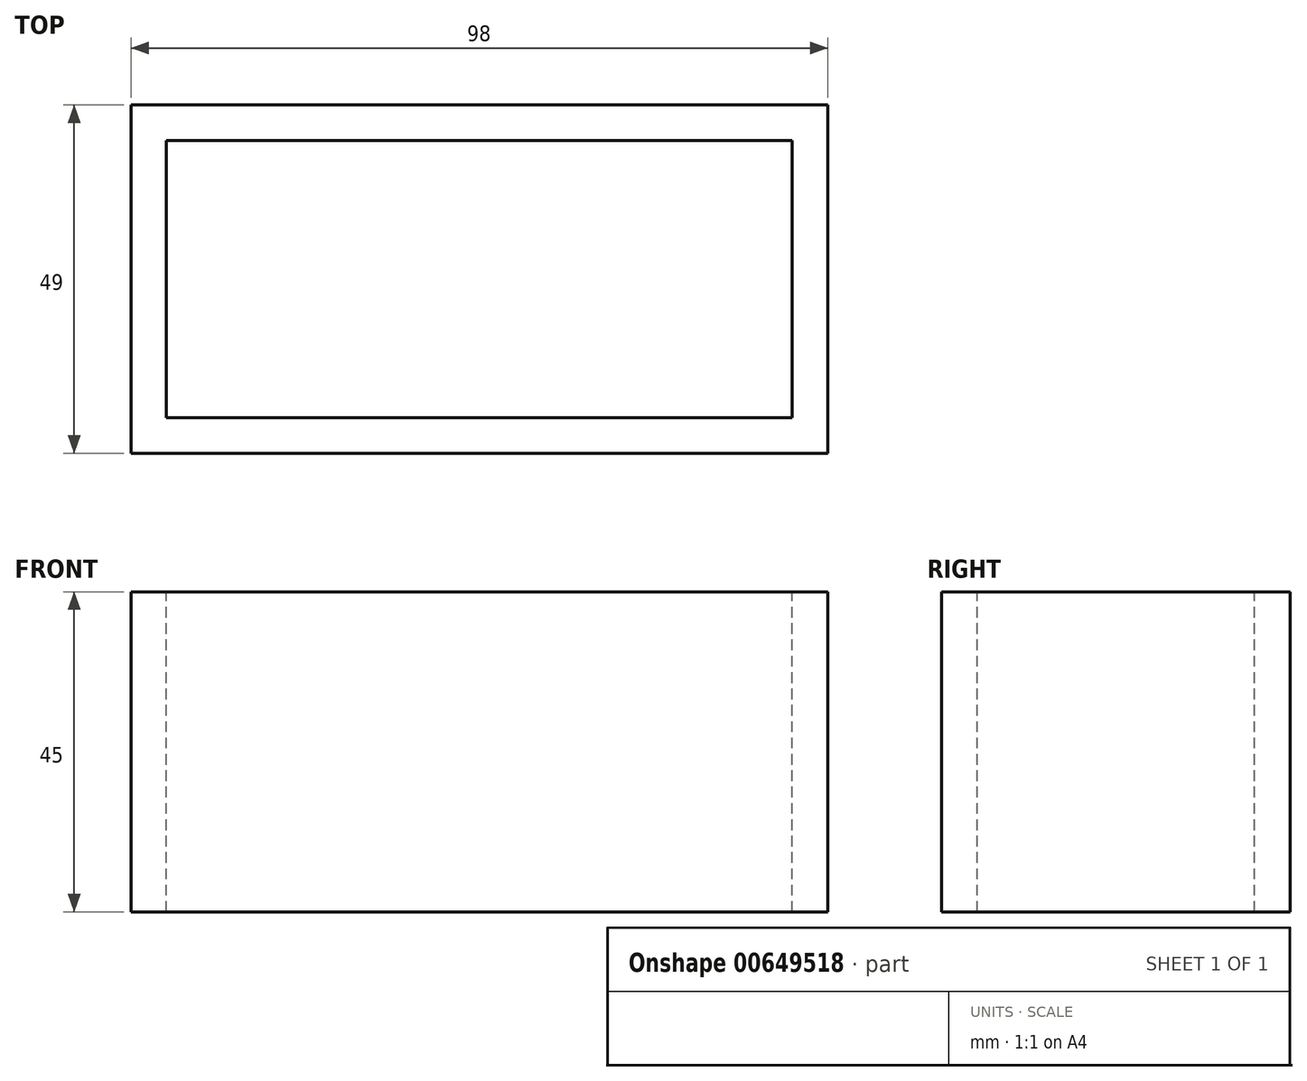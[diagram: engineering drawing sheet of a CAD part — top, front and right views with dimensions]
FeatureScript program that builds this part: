
annotation { "Feature Type Name" : "Feature", "Feature Type Description" : "" }
export const myFeature = defineFeature(function(context is Context, id is Id, definition is map)
    precondition{}
    {
        {
            var Q0;
            Q0=qCreatedBy(makeId("Top.planeOp"),FACE);
            var sketch = newSketch(context, id + "F0", { "sketchPlane" : qUnion([Q0])});
            skLineSegment(sketch, "E0.bottom", {"start": v(-44, 19.5) * mm, "end": v(44, 19.5) * mm});
            skLineSegment(sketch, "E0.top", {"start": v(-44, -19.5) * mm, "end": v(44, -19.5) * mm});
            skLineSegment(sketch, "E0.left", {"start": v(-44, 19.5) * mm, "end": v(-44, -19.5) * mm});
            skLineSegment(sketch, "E0.right", {"start": v(44, 19.5) * mm, "end": v(44, -19.5) * mm});
            skPoint(sketch, "E0.middle", {"position": v(0, 0) * mm});
            skLineSegment(sketch, "E1.bottom", {"start": v(-49, 24.5) * mm, "end": v(49, 24.5) * mm});
            skLineSegment(sketch, "E1.top", {"start": v(-49, -24.5) * mm, "end": v(49, -24.5) * mm});
            skLineSegment(sketch, "E1.left", {"start": v(-49, 24.5) * mm, "end": v(-49, -24.5) * mm});
            skLineSegment(sketch, "E1.right", {"start": v(49, 24.5) * mm, "end": v(49, -24.5) * mm});
            skSolve(sketch);
        }
        {
            var Q0;
            Q0=sQuery(id+"F0.wireOp",EDGE,"E1.top");
            var Q1;
            Q1=sQuery(id+"F0.wireOp",EDGE,"E0.left");
            var Q2;
            Q2=sQuery(id+"F0.wireOp",EDGE,"E1.left");
            var Q3;
            Q3=sQuery(id+"F0.wireOp",EDGE,"E0.top");
            var Q4;
            Q4=sQuery(id+"F0.wireOp",EDGE,"E0.right");
            var Q5;
            Q5=sQuery(id+"F0.wireOp",EDGE,"E0.bottom");
            var Q6;
            Q6=sQuery(id+"F0.wireOp",EDGE,"E1.bottom");
            var Q7;
            Q7=sQuery(id+"F0.wireOp",EDGE,"E1.right");
            extrude(context, id + "F1", {"bodyType" : ToolBodyType.SURFACE, "surfaceEntities" : qUnion([Q0, Q1, Q2, Q3, Q4, Q5, Q6, Q7]), "depth" : 45 * mm, "offsetDistance" : 25.4 * mm});
        }
    });
